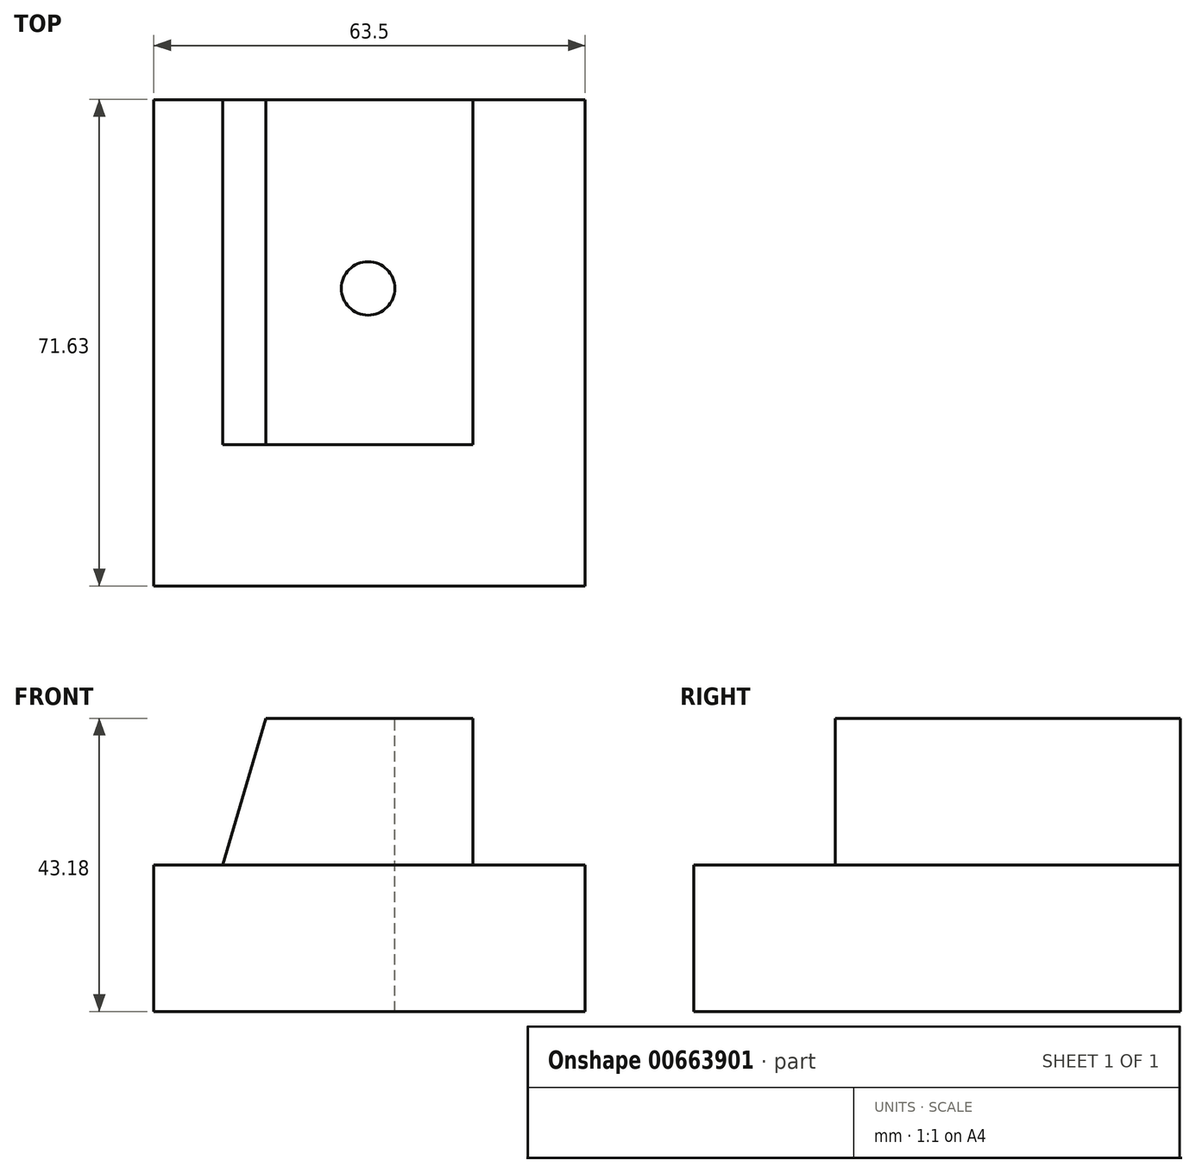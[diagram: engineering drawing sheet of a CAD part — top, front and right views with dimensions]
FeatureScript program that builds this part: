
annotation { "Feature Type Name" : "Feature", "Feature Type Description" : "" }
export const myFeature = defineFeature(function(context is Context, id is Id, definition is map)
    precondition{}
    {
        {
            var Q0;
            Q0=qCreatedBy(makeId("Top.planeOp"),FACE);
            var sketch = newSketch(context, id + "F0", { "sketchPlane" : qUnion([Q0])});
            skLineSegment(sketch, "E0.bottom", {"start": v(0, 0) * mm, "end": v(63.5, 0) * mm});
            skLineSegment(sketch, "E0.top", {"start": v(0, 71.63) * mm, "end": v(63.5, 71.63) * mm});
            skLineSegment(sketch, "E0.left", {"start": v(0, 0) * mm, "end": v(0, 71.63) * mm});
            skLineSegment(sketch, "E0.right", {"start": v(63.5, 0) * mm, "end": v(63.5, 71.63) * mm});
            skSolve(sketch);
        }
        {
            var Q0;
            Q0 = qSketchRegion(id + "F0", true);
            extrude(context, id + "F1", {"entities" : qUnion([Q0]), "oppositeDirection" : true, "depth" : 21.59 * mm, "offsetDistance" : 25.4 * mm});
        }
        {
            var Q0;
            Q0=makeQuery(id+"F1.opExtrude","CAP_FACE",FACE,{"disambiguationData":[OSD([sQuery(id+"F0.wireOp",EDGE,"E0.bottom"),sQuery(id+"F0.wireOp",EDGE,"E0.top"),sQuery(id+"F0.wireOp",EDGE,"E0.left"),sQuery(id+"F0.wireOp",EDGE,"E0.right")])],"isStart":true});
            var sketch = newSketch(context, id + "F2", { "sketchPlane" : qUnion([Q0])});
            skLineSegment(sketch, "E1.bottom", {"start": v(10.16, 71.63) * mm, "end": v(46.99, 71.63) * mm});
            skLineSegment(sketch, "E1.top", {"start": v(10.16, 20.83) * mm, "end": v(46.99, 20.83) * mm});
            skLineSegment(sketch, "E1.left", {"start": v(10.16, 71.63) * mm, "end": v(10.16, 20.83) * mm});
            skLineSegment(sketch, "E1.right", {"start": v(46.99, 71.63) * mm, "end": v(46.99, 20.83) * mm});
            skSolve(sketch);
        }
        {
            var Q0;
            Q0=makeQuery(id+"F2.imprint","IMPRINT",FACE,{"disambiguationData":[TD([[makeQuery(id+"F2.imprint","IMPRINT",EDGE,{"derivedFrom":sQuery(id+"F2.wireOp",EDGE,"E1.bottom")}),-1.0]])]});
            extrude(context, id + "F3", {"entities" : qUnion([Q0]), "operationType" : NewBodyOperationType.ADD, "depth" : 21.59 * mm, "offsetDistance" : 25.4 * mm});
        }
        {
            var Q0;
            Q0=makeQuery(id+"F3.opExtrude","SWEPT_FACE",FACE,{"disambiguationData":[OSD([sQuery(id+"F2.wireOp",EDGE,"E1.top")])]});
            var sketch = newSketch(context, id + "F4", { "sketchPlane" : qUnion([Q0])});
            skLineSegment(sketch, "E2", {"start": v(46.99, 21.59) * mm, "end": v(16.5, 21.59) * mm});
            skLineSegment(sketch, "E3", {"start": v(16.5, 21.59) * mm, "end": v(10.16, 0) * mm});
            skLineSegment(sketch, "E4", {"start": v(10.16, 0) * mm, "end": v(46.99, 0) * mm});
            skLineSegment(sketch, "E5", {"start": v(46.99, 0) * mm, "end": v(46.99, 21.59) * mm});
            skSolve(sketch);
        }
        {
            var Q0;
            {var subQ0=sQuery(id+"F4.wireOp",EDGE,"E3");Q0=makeQuery(id+"F4.imprint","IMPRINT",FACE,{"disambiguationData":[TD([[makeQuery(id+"F4.imprint","IMPRINT",EDGE,{"derivedFrom":subQ0}),-1.0]])]});}
            extrude(context, id + "F5", {"entities" : qUnion([Q0]), "operationType" : NewBodyOperationType.REMOVE, "oppositeDirection" : true, "depth" : 50.8 * mm, "offsetDistance" : 25.4 * mm});
        }
        {
            var Q0;
            Q0=makeQuery(id+"F3.opExtrude","CAP_FACE",FACE,{"disambiguationData":[OSD([sQuery(id+"F2.wireOp",EDGE,"E1.bottom"),sQuery(id+"F2.wireOp",EDGE,"E1.top"),sQuery(id+"F2.wireOp",EDGE,"E1.left"),sQuery(id+"F2.wireOp",EDGE,"E1.right")])],"isStart":false});
            var sketch = newSketch(context, id + "F6", { "sketchPlane" : qUnion([Q0])});
            skCircle(sketch, "E6", {"center": v(31.55, 43.81) * mm, "radius": 3.94 * mm});
            skSolve(sketch);
        }
        {
            var Q0;
            Q0=makeQuery(id+"F6.imprint","IMPRINT",FACE,{"disambiguationData":[TD([[makeQuery(id+"F6.imprint","IMPRINT",EDGE,{"derivedFrom":sQuery(id+"F6.wireOp",EDGE,"E6")}),1.0]])]});
            extrude(context, id + "F7", {"entities" : qUnion([Q0]), "operationType" : NewBodyOperationType.REMOVE, "endBound" : BoundingType.THROUGH_ALL, "oppositeDirection" : true, "depth" : 25.4 * mm, "offsetDistance" : 25.4 * mm});
        }
    });
